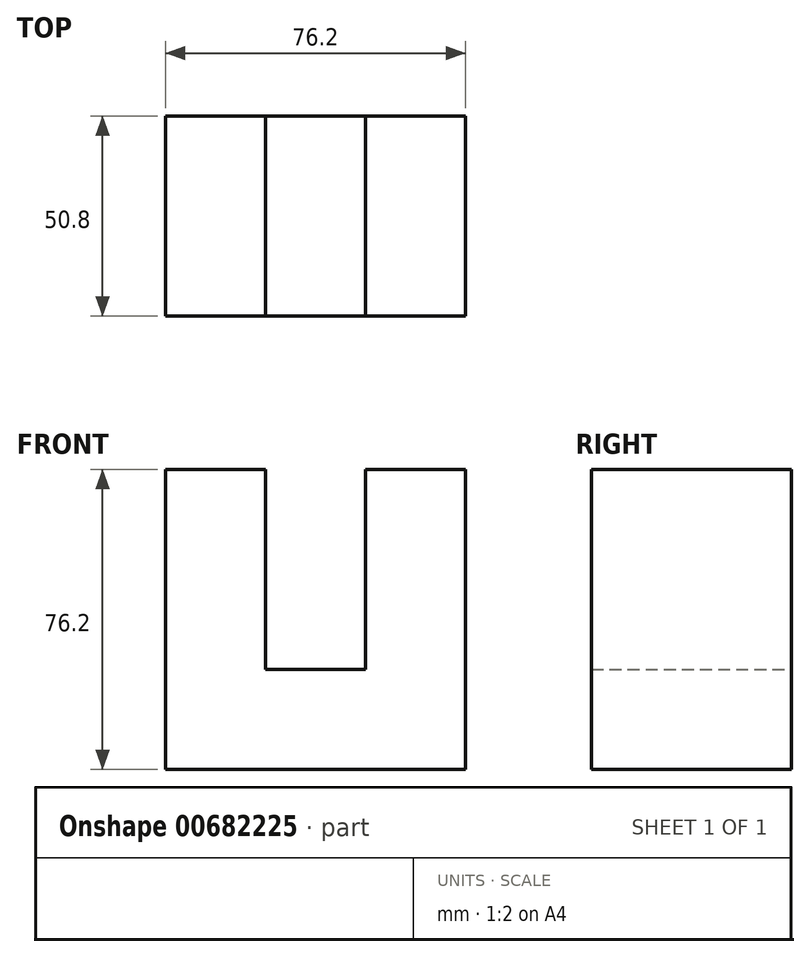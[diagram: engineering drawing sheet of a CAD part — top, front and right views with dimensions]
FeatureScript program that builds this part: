
annotation { "Feature Type Name" : "Feature", "Feature Type Description" : "" }
export const myFeature = defineFeature(function(context is Context, id is Id, definition is map)
    precondition{}
    {
        {
            var Q0;
            Q0=qCreatedBy(makeId("Front.planeOp"),FACE);
            var sketch = newSketch(context, id + "F0", { "sketchPlane" : qUnion([Q0])});
            skLineSegment(sketch, "E0", {"start": v(-25.94, -50.3) * mm, "end": v(50.26, -50.3) * mm});
            skLineSegment(sketch, "E1", {"start": v(-25.94, -50.3) * mm, "end": v(-25.94, 25.9) * mm});
            skLineSegment(sketch, "E2", {"start": v(-25.94, 25.9) * mm, "end": v(-0.54, 25.9) * mm});
            skLineSegment(sketch, "E3", {"start": v(-0.54, 25.9) * mm, "end": v(-0.54, -24.9) * mm});
            skLineSegment(sketch, "E4", {"start": v(-0.54, -24.9) * mm, "end": v(24.86, -24.9) * mm});
            skLineSegment(sketch, "E5", {"start": v(24.86, -24.9) * mm, "end": v(24.86, 25.9) * mm});
            skLineSegment(sketch, "E6", {"start": v(24.86, 25.9) * mm, "end": v(50.26, 25.9) * mm});
            skLineSegment(sketch, "E7", {"start": v(50.26, 25.9) * mm, "end": v(50.26, -50.3) * mm});
            skSolve(sketch);
        }
        {
            var Q0;
            Q0=makeQuery(id+"F0.imprint","IMPRINT",FACE,{"disambiguationData":[TD([[makeQuery(id+"F0.imprint","IMPRINT",EDGE,{"derivedFrom":sQuery(id+"F0.wireOp",EDGE,"E0")}),1.0]])]});
            extrude(context, id + "F1", {"entities" : qUnion([Q0]), "depth" : 50.8 * mm, "offsetDistance" : 25.4 * mm});
        }
    });
